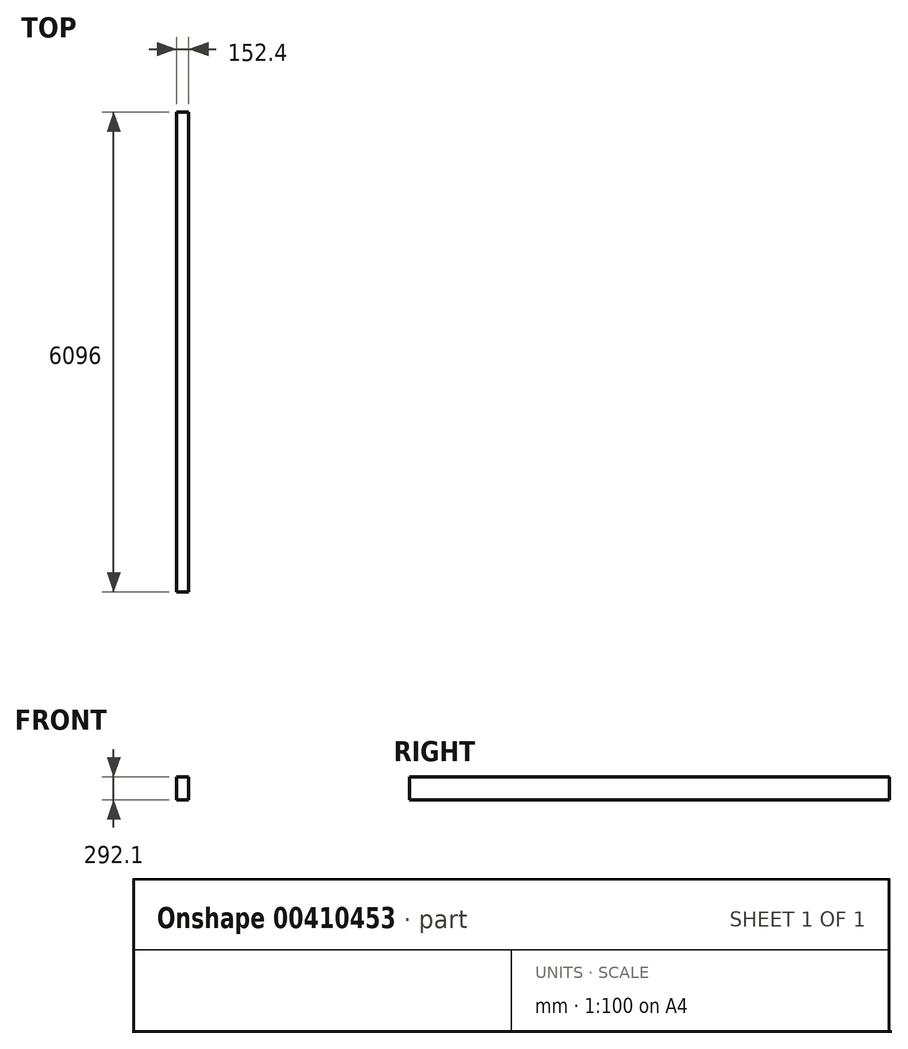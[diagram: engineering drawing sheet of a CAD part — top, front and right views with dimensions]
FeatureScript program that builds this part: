
annotation { "Feature Type Name" : "Feature", "Feature Type Description" : "" }
export const myFeature = defineFeature(function(context is Context, id is Id, definition is map)
    precondition{}
    {
        {
            var Q0;
            Q0=qCreatedBy(makeId("Right.planeOp"),FACE);
            var sketch = newSketch(context, id + "F0", { "sketchPlane" : qUnion([Q0])});
            skLineSegment(sketch, "E0.bottom", {"start": v(-3048, 146.05) * mm, "end": v(3048, 146.05) * mm});
            skLineSegment(sketch, "E0.top", {"start": v(-3048, -146.05) * mm, "end": v(3048, -146.05) * mm});
            skLineSegment(sketch, "E0.left", {"start": v(-3048, 146.05) * mm, "end": v(-3048, -146.05) * mm});
            skLineSegment(sketch, "E0.right", {"start": v(3048, 146.05) * mm, "end": v(3048, -146.05) * mm});
            skPoint(sketch, "E0.middle", {"position": v(0, 0) * mm});
            skSolve(sketch);
        }
        {
            var Q0;
            Q0 = qSketchRegion(id + "F0", true);
            extrude(context, id + "F1", {"entities" : qUnion([Q0]), "depth" : 152.4 * mm, "offsetDistance" : 25.4 * mm});
        }
    });
